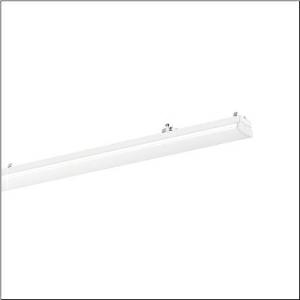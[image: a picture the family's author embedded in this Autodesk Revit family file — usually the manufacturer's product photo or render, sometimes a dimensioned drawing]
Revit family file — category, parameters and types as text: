
# Revit family: licross_r__21_recessed_opal_ho_52te1ddn4e5m_caad
name_source: partatom
category: Lighting Fixtures
units: mm (PartAtom-declared; Revit-internal decimal feet)

## family parameters
Cut with Voids When Loaded = No
Host = Face
Light Source = No
Part Type = Normal
Room Calculation Point = No
Round Connector Dimension = Use Diameter
Shared = No

## types (1)
- --- (1 x LED, 14560 lm, 84.6 W, 4000K)
    Apparent Load = 85 VA
    CIE Flux Codes = 44 73 91 87 100
    Color Rendering = 80
    Color Temperature = 4000K
    Default Elevation = 1800 mm
    Description = Licross® 21 recessed opal HO, luminaire insert, of sheet steel, galvanised, coil coated, white, length: 1.500mm, width: 66mm, height: 67mm, LED rated luminous flux: 14.560lm, light colour: 840, control gear: DALI 2, with plug, 5-pole, with phase selection, mains connection: 220..240V, AC, 50/60Hz, rated input power: 85W, internal wiring halogen-free, primary optical cover: cover, of PMMA, light emission: direct with ceiling illumination distribution, primary light characteristic: symmetric, protection rating (complete): IP54, insulation class (complete): insulation class I (protective earthing), certification: CE, ENEC, VDE, UKCA, protection symbol: D if used in an environment with non-conductive dust loads with corresponding accessories, impact resistance: IK06, permissible ambient temperature for indoor applications: -25..+30°C, corresponds to IFS (International Featured Standards) requirements for safety and quality in the food industry, reducing of maximum allowable ambient temperature of 5°C with ceiling mounting, LABS conformity tested according to VDMA 24364:2018-05, packaging unit: 1 piece
    Height = 83 mm
    Lamp = 1 x LED
    Lamp Light Flux = 14560 lm
    Lamp Power = 84.6 W
    Lamp count = 1
    Length = 1500 mm
    Luminous efficacy = 172 lm/W
    Manufacturer = Siteco
    ModVariant = No
    Model = 52TE1DDN4E5M
    Mounting Place = Ceiling
    Mounting Type = Pendant
    Number of Poles = 1
    OnlyDefault = Yes
    Power Factor = 1
    Product Name = Licross® 21 recessed opal HO
    Product group = luminaire insert | ceiling pendant
    ProductGroupID = 902
    Protection Class = Protection class I
    Protection Degree = IP 54
    RLX_Detail_Level = 1
    RLX_Emergency_Light_Flux = 0 lm
    RLX_Emergency_Type = 0
    RLX_Emergency_Type_DB = No
    RlxData = <blob elided: 27101 chars, md5=61e28be1>
    Socket = socket
    Standby Power = 0 W
    System Light Flux = 14560 lm
    System Power = 85 W
    Type Comments = factory setting: luminous flux: 100 % | dim-lin: 254 | 484 mA
    Type Image = l_1313666.jpg
    URL = http://relux.com
    VarID = @adj_089985
    Voltage = 0 V
    Weight = 0.00 kg
    Width = 76 mm

## geometry (parser evidence)
native form markers: Blend x4, Sweep x12
no freeform markers — native parametric forms only
